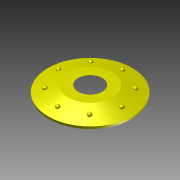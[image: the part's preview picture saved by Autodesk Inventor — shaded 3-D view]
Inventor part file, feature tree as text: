
AUTODESK INVENTOR PART (.ipt)
format: ipt  version: 2011 (Build 150239000, 239)  size: 122,368 bytes
history: native  units: in
note: dims shown in document units (in); Inventor stores cm internally (conversion verified against a paired STEP export)
features: revolve x2, sketch x2, plane x1, pattern_circular x1
ambient origin geometry x8: Origin, YZ Plane, XZ Plane, XY Plane, X Axis, Y Axis, Z Axis, Center Point
bodies: Solid1 (feature_tree)
feature tree (6):
  revolve  "Revolution1"  Angle=90.0deg
  plane  "Work Plane1"
  revolve  "Revolution2"  [1 undecoded]
  pattern_circular  "Circular Pattern1"  [2 undecoded]
  sketch  "Sketch1"  dims[d0=1.0in d1=90.0deg]
  sketch  "Sketch2"  dims[d2=0.875in d3=0.0in d6=0.25in d7=0.25in d8=90.0deg d9=3.1496in d10=360.0deg]
note: 3 required parameter values undecoded (feature->parameter linkage not recoverable at this tier; creation-order binding heuristic only, values carry confidence <= 0.55)